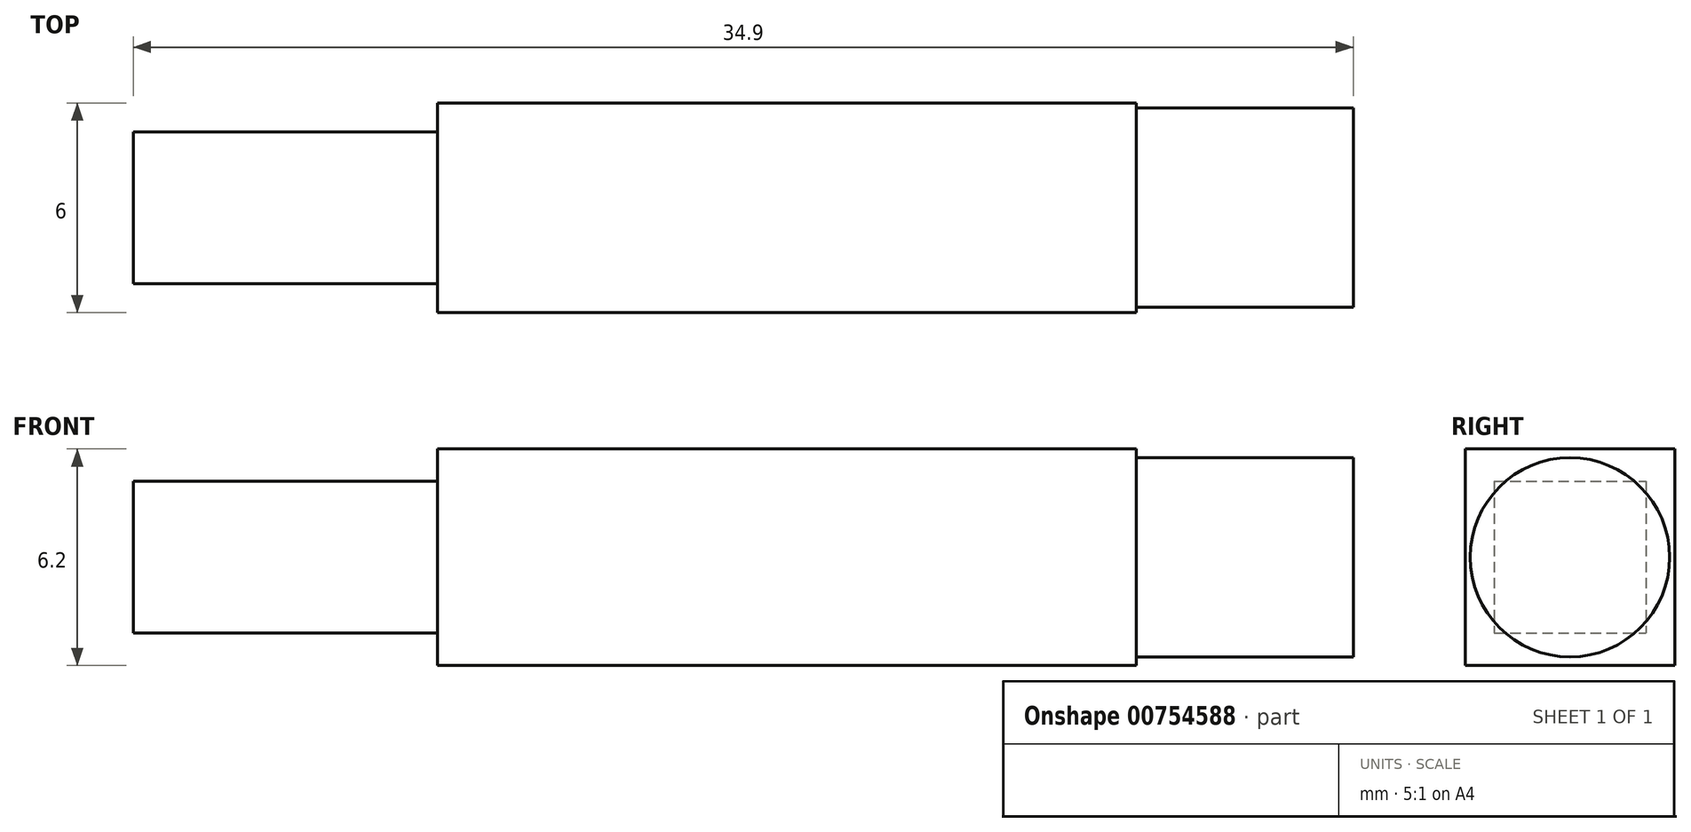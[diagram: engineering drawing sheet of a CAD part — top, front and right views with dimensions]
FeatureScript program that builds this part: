
annotation { "Feature Type Name" : "Feature", "Feature Type Description" : "" }
export const myFeature = defineFeature(function(context is Context, id is Id, definition is map)
    precondition{}
    {
        {
            var Q0;
            Q0=qCreatedBy(makeId("Right.planeOp"),FACE);
            var sketch = newSketch(context, id + "F0", { "sketchPlane" : qUnion([Q0])});
            skLineSegment(sketch, "E0.top", {"start": v(-3, -6.2) * mm, "end": v(3, -6.2) * mm});
            skLineSegment(sketch, "E0.left", {"start": v(-3, 0) * mm, "end": v(-3, -6.2) * mm});
            skLineSegment(sketch, "E0.right", {"start": v(3, 0) * mm, "end": v(3, -6.2) * mm});
            skLineSegment(sketch, "E1.top", {"start": v(-1.85, 1.9) * mm, "end": v(1.85, 1.9) * mm});
            skLineSegment(sketch, "E1.left", {"start": v(-1.85, 0) * mm, "end": v(-1.85, 1.9) * mm});
            skLineSegment(sketch, "E1.right", {"start": v(1.85, 0) * mm, "end": v(1.85, 1.9) * mm});
            skLineSegment(sketch, "E2", {"start": v(-3, 0) * mm, "end": v(3, 0) * mm});
            skLineSegment(sketch, "E3", {"start": v(-1.85, 0) * mm, "end": v(1.85, 0) * mm});
            skLineSegment(sketch, "E4", {"start": v(-3, 0) * mm, "end": v(3, -6.2) * mm, "construction": true});
            skPoint(sketch, "E5", {"position": v(0, -3.1) * mm});
            skSolve(sketch);
        }
        {
            var Q0;
            Q0=makeQuery(id+"F0.imprint","IMPRINT",FACE,{"disambiguationData":[TD([[makeQuery(id+"F0.imprint","IMPRINT",EDGE,{"derivedFrom":sQuery(id+"F0.wireOp",EDGE,"E0.top")}),1.0]])]});
            extrude(context, id + "F1", {"entities" : qUnion([Q0]), "oppositeDirection" : true, "depth" : 20 * mm, "offsetDistance" : 25 * mm});
        }
        {
            var Q0;
            Q0=makeQuery(id+"F1.opExtrude","CAP_FACE",FACE,{"disambiguationData":[OSD([sQuery(id+"F0.wireOp",EDGE,"E0.top"),sQuery(id+"F0.wireOp",EDGE,"E0.left"),sQuery(id+"F0.wireOp",EDGE,"E0.right"),sQuery(id+"F0.wireOp",EDGE,"E2")])],"isStart":true});
            var sketch = newSketch(context, id + "F2", { "sketchPlane" : qUnion([Q0])});
            skCircle(sketch, "E6", {"center": v(0, -3.1) * mm, "radius": 2.85 * mm});
            skPoint(sketch, "E6.centerSnap0", {"position": v(3, -3.1) * mm});
            skSolve(sketch);
        }
        {
            var Q0;
            Q0=makeQuery(id+"F2.imprint","IMPRINT",FACE,{"disambiguationData":[TD([[makeQuery(id+"F2.imprint","IMPRINT",EDGE,{"derivedFrom":sQuery(id+"F2.wireOp",EDGE,"E6")}),1.0]])]});
            var Q1;
            Q1=sQuery(id+"F2.wireOp",EDGE,"E6");
            extrude(context, id + "F3", {"entities" : qUnion([Q0]), "operationType" : NewBodyOperationType.ADD, "surfaceEntities" : qUnion([Q1]), "depth" : 6.2 * mm, "offsetDistance" : 25 * mm});
        }
        {
            var Q0;
            Q0=makeQuery(id+"F1.opExtrude","CAP_FACE",FACE,{"disambiguationData":[OSD([sQuery(id+"F0.wireOp",EDGE,"E0.top"),sQuery(id+"F0.wireOp",EDGE,"E0.left"),sQuery(id+"F0.wireOp",EDGE,"E0.right"),sQuery(id+"F0.wireOp",EDGE,"E2")])],"isStart":false});
            var sketch = newSketch(context, id + "F4", { "sketchPlane" : qUnion([Q0])});
            skLineSegment(sketch, "E7.bottom", {"start": v(2.17, -0.93) * mm, "end": v(-2.17, -0.93) * mm});
            skLineSegment(sketch, "E7.top", {"start": v(2.17, -5.27) * mm, "end": v(-2.17, -5.27) * mm});
            skLineSegment(sketch, "E7.left", {"start": v(2.17, -0.93) * mm, "end": v(2.17, -5.27) * mm});
            skLineSegment(sketch, "E7.right", {"start": v(-2.17, -0.93) * mm, "end": v(-2.17, -5.27) * mm});
            skPoint(sketch, "E7.middle", {"position": v(0, -3.1) * mm});
            skPoint(sketch, "E7.middle.positionSnap0", {"position": v(-3, -3.1) * mm});
            skPoint(sketch, "E7.middle.positionSnap1", {"position": v(0, 0) * mm});
            skPoint(sketch, "E7.centerSnap0", {"position": v(-3, -3.1) * mm});
            skPoint(sketch, "E7.centerSnap1", {"position": v(0, 0) * mm});
            skSolve(sketch);
        }
        {
            var Q0;
            Q0=makeQuery(id+"F4.imprint","IMPRINT",FACE,{"disambiguationData":[TD([[makeQuery(id+"F4.imprint","IMPRINT",EDGE,{"derivedFrom":sQuery(id+"F4.wireOp",EDGE,"E7.bottom")}),1.0]])]});
            extrude(context, id + "F5", {"entities" : qUnion([Q0]), "operationType" : NewBodyOperationType.ADD, "depth" : 8.7 * mm, "offsetDistance" : 25 * mm});
        }
    });
